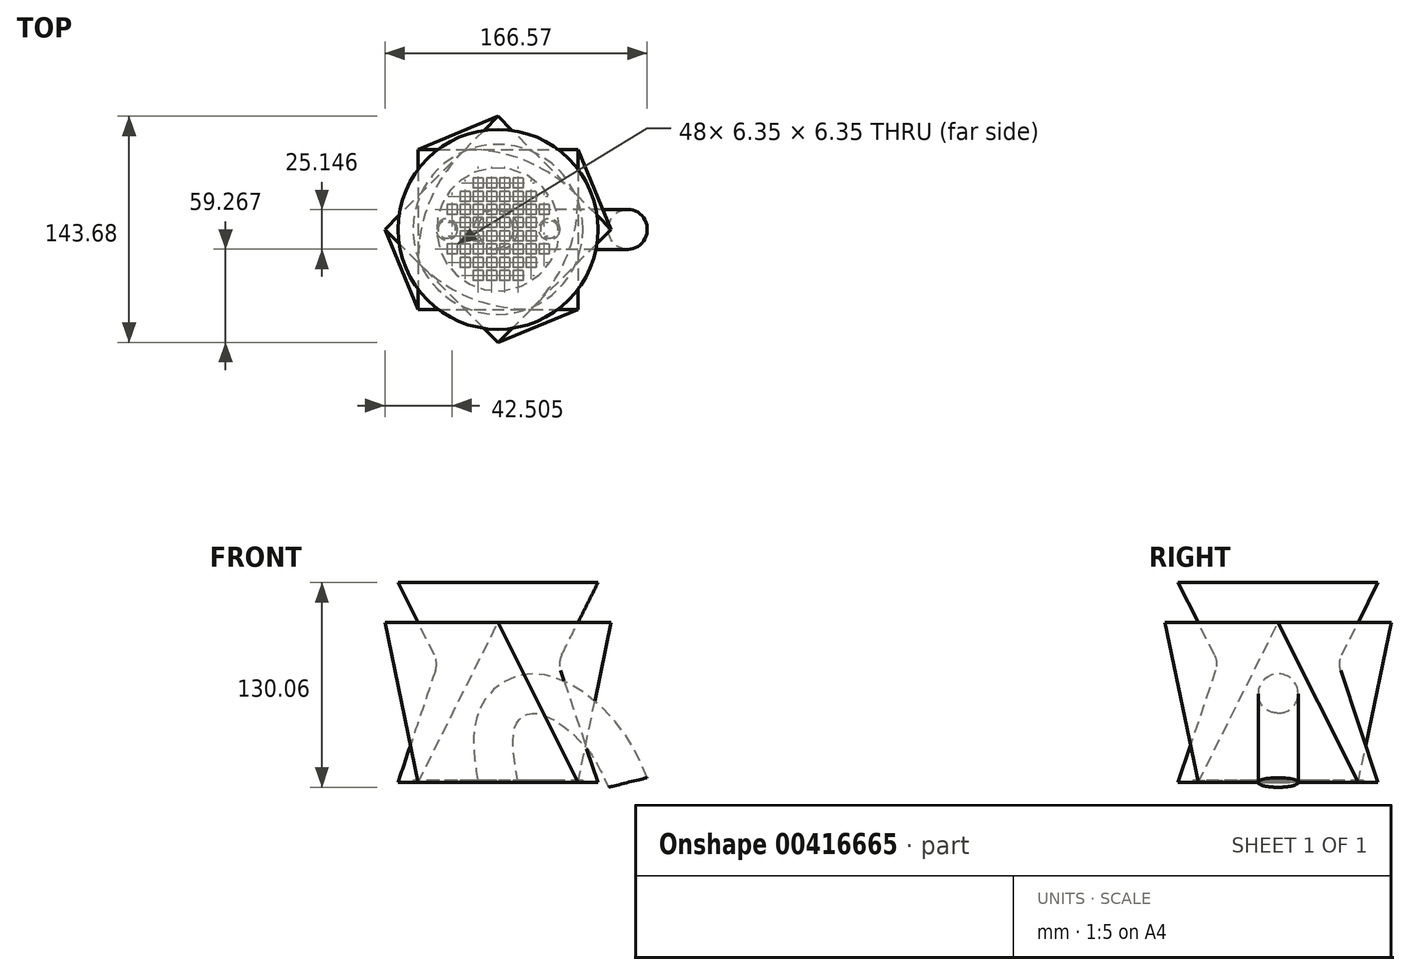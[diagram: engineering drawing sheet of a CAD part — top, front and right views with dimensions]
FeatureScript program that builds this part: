
annotation { "Feature Type Name" : "Feature", "Feature Type Description" : "" }
export const myFeature = defineFeature(function(context is Context, id is Id, definition is map)
    precondition{}
    {
        {
            var Q0;
            Q0=qCreatedBy(makeId("Top.planeOp"),FACE);
            var sketch = newSketch(context, id + "F0", { "sketchPlane" : qUnion([Q0])});
            skCircle(sketch, "E0", {"center": v(0, 0) * mm, "radius": 53.98 * mm});
            skPoint(sketch, "E1.middle", {"position": v(0, 6.35) * mm});
            skPoint(sketch, "E2.middle", {"position": v(-29.34, -29.34) * mm});
            skLineSegment(sketch, "E3.0.2.0", {"start": v(-26.16, -9.4) * mm, "end": v(-26.16, -15.75) * mm});
            skLineSegment(sketch, "E3.0.2.1", {"start": v(-26.16, -9.4) * mm, "end": v(-32.51, -9.4) * mm});
            skLineSegment(sketch, "E3.0.2.2", {"start": v(-32.51, -9.4) * mm, "end": v(-32.51, -15.75) * mm});
            skLineSegment(sketch, "E3.0.2.3", {"start": v(-26.16, -15.75) * mm, "end": v(-32.51, -15.75) * mm});
            skLineSegment(sketch, "E3.0.5.0", {"start": v(-26.16, 15.75) * mm, "end": v(-26.16, 9.4) * mm});
            skLineSegment(sketch, "E3.0.5.1", {"start": v(-26.16, 15.75) * mm, "end": v(-32.51, 15.75) * mm});
            skLineSegment(sketch, "E3.0.5.2", {"start": v(-32.51, 15.75) * mm, "end": v(-32.51, 9.4) * mm});
            skLineSegment(sketch, "E3.0.5.3", {"start": v(-26.16, 9.4) * mm, "end": v(-32.51, 9.4) * mm});
            skLineSegment(sketch, "E3.1.1.0", {"start": v(-17.78, -17.78) * mm, "end": v(-17.78, -24.13) * mm});
            skLineSegment(sketch, "E3.1.1.1", {"start": v(-17.78, -17.78) * mm, "end": v(-24.13, -17.78) * mm});
            skLineSegment(sketch, "E3.1.1.2", {"start": v(-24.13, -17.78) * mm, "end": v(-24.13, -24.13) * mm});
            skLineSegment(sketch, "E3.1.1.3", {"start": v(-17.78, -24.13) * mm, "end": v(-24.13, -24.13) * mm});
            skLineSegment(sketch, "E3.1.2.0", {"start": v(-17.78, -9.4) * mm, "end": v(-17.78, -15.75) * mm});
            skLineSegment(sketch, "E3.1.2.1", {"start": v(-17.78, -9.4) * mm, "end": v(-24.13, -9.4) * mm});
            skLineSegment(sketch, "E3.1.2.2", {"start": v(-24.13, -9.4) * mm, "end": v(-24.13, -15.75) * mm});
            skLineSegment(sketch, "E3.1.2.3", {"start": v(-17.78, -15.75) * mm, "end": v(-24.13, -15.75) * mm});
            skLineSegment(sketch, "E3.1.3.0", {"start": v(-17.78, -1.02) * mm, "end": v(-17.78, -7.37) * mm});
            skLineSegment(sketch, "E3.1.3.1", {"start": v(-17.78, -1.02) * mm, "end": v(-24.13, -1.02) * mm});
            skLineSegment(sketch, "E3.1.3.2", {"start": v(-24.13, -1.02) * mm, "end": v(-24.13, -7.37) * mm});
            skLineSegment(sketch, "E3.1.3.3", {"start": v(-17.78, -7.37) * mm, "end": v(-24.13, -7.37) * mm});
            skLineSegment(sketch, "E3.1.4.0", {"start": v(-17.78, 7.37) * mm, "end": v(-17.78, 1.02) * mm});
            skLineSegment(sketch, "E3.1.4.1", {"start": v(-17.78, 7.37) * mm, "end": v(-24.13, 7.37) * mm});
            skLineSegment(sketch, "E3.1.4.2", {"start": v(-24.13, 7.37) * mm, "end": v(-24.13, 1.02) * mm});
            skLineSegment(sketch, "E3.1.4.3", {"start": v(-17.78, 1.02) * mm, "end": v(-24.13, 1.02) * mm});
            skLineSegment(sketch, "E3.1.5.0", {"start": v(-17.78, 15.75) * mm, "end": v(-17.78, 9.4) * mm});
            skLineSegment(sketch, "E3.1.5.1", {"start": v(-17.78, 15.75) * mm, "end": v(-24.13, 15.75) * mm});
            skLineSegment(sketch, "E3.1.5.2", {"start": v(-24.13, 15.75) * mm, "end": v(-24.13, 9.4) * mm});
            skLineSegment(sketch, "E3.1.5.3", {"start": v(-17.78, 9.4) * mm, "end": v(-24.13, 9.4) * mm});
            skLineSegment(sketch, "E3.1.6.0", {"start": v(-17.78, 24.13) * mm, "end": v(-17.78, 17.78) * mm});
            skLineSegment(sketch, "E3.1.6.1", {"start": v(-17.78, 24.13) * mm, "end": v(-24.13, 24.13) * mm});
            skLineSegment(sketch, "E3.1.6.2", {"start": v(-24.13, 24.13) * mm, "end": v(-24.13, 17.78) * mm});
            skLineSegment(sketch, "E3.1.6.3", {"start": v(-17.78, 17.78) * mm, "end": v(-24.13, 17.78) * mm});
            skLineSegment(sketch, "E3.2.0.0", {"start": v(-9.4, -26.16) * mm, "end": v(-9.4, -32.51) * mm});
            skLineSegment(sketch, "E3.2.0.1", {"start": v(-9.4, -26.16) * mm, "end": v(-15.75, -26.16) * mm});
            skLineSegment(sketch, "E3.2.0.2", {"start": v(-15.75, -26.16) * mm, "end": v(-15.75, -32.51) * mm});
            skLineSegment(sketch, "E3.2.0.3", {"start": v(-9.4, -32.51) * mm, "end": v(-15.75, -32.51) * mm});
            skLineSegment(sketch, "E3.2.1.0", {"start": v(-9.4, -17.78) * mm, "end": v(-9.4, -24.13) * mm});
            skLineSegment(sketch, "E3.2.1.1", {"start": v(-9.4, -17.78) * mm, "end": v(-15.75, -17.78) * mm});
            skLineSegment(sketch, "E3.2.1.2", {"start": v(-15.75, -17.78) * mm, "end": v(-15.75, -24.13) * mm});
            skLineSegment(sketch, "E3.2.1.3", {"start": v(-9.4, -24.13) * mm, "end": v(-15.75, -24.13) * mm});
            skLineSegment(sketch, "E3.2.2.0", {"start": v(-9.4, -9.4) * mm, "end": v(-9.4, -15.75) * mm});
            skLineSegment(sketch, "E3.2.2.1", {"start": v(-9.4, -9.4) * mm, "end": v(-15.75, -9.4) * mm});
            skLineSegment(sketch, "E3.2.2.2", {"start": v(-15.75, -9.4) * mm, "end": v(-15.75, -15.75) * mm});
            skLineSegment(sketch, "E3.2.2.3", {"start": v(-9.4, -15.75) * mm, "end": v(-15.75, -15.75) * mm});
            skLineSegment(sketch, "E3.2.3.0", {"start": v(-9.4, -1.02) * mm, "end": v(-9.4, -7.37) * mm});
            skLineSegment(sketch, "E3.2.3.1", {"start": v(-9.4, -1.02) * mm, "end": v(-15.75, -1.02) * mm});
            skLineSegment(sketch, "E3.2.3.2", {"start": v(-15.75, -1.02) * mm, "end": v(-15.75, -7.37) * mm});
            skLineSegment(sketch, "E3.2.3.3", {"start": v(-9.4, -7.37) * mm, "end": v(-15.75, -7.37) * mm});
            skLineSegment(sketch, "E3.2.4.0", {"start": v(-9.4, 7.37) * mm, "end": v(-9.4, 1.02) * mm});
            skLineSegment(sketch, "E3.2.4.1", {"start": v(-9.4, 7.37) * mm, "end": v(-15.75, 7.37) * mm});
            skLineSegment(sketch, "E3.2.4.2", {"start": v(-15.75, 7.37) * mm, "end": v(-15.75, 1.02) * mm});
            skLineSegment(sketch, "E3.2.4.3", {"start": v(-9.4, 1.02) * mm, "end": v(-15.75, 1.02) * mm});
            skLineSegment(sketch, "E3.2.5.0", {"start": v(-9.4, 15.75) * mm, "end": v(-9.4, 9.4) * mm});
            skLineSegment(sketch, "E3.2.5.1", {"start": v(-9.4, 15.75) * mm, "end": v(-15.75, 15.75) * mm});
            skLineSegment(sketch, "E3.2.5.2", {"start": v(-15.75, 15.75) * mm, "end": v(-15.75, 9.4) * mm});
            skLineSegment(sketch, "E3.2.5.3", {"start": v(-9.4, 9.4) * mm, "end": v(-15.75, 9.4) * mm});
            skLineSegment(sketch, "E3.2.6.0", {"start": v(-9.4, 24.13) * mm, "end": v(-9.4, 17.78) * mm});
            skLineSegment(sketch, "E3.2.6.1", {"start": v(-9.4, 24.13) * mm, "end": v(-15.75, 24.13) * mm});
            skLineSegment(sketch, "E3.2.6.2", {"start": v(-15.75, 24.13) * mm, "end": v(-15.75, 17.78) * mm});
            skLineSegment(sketch, "E3.2.6.3", {"start": v(-9.4, 17.78) * mm, "end": v(-15.75, 17.78) * mm});
            skLineSegment(sketch, "E3.2.7.0", {"start": v(-9.4, 32.51) * mm, "end": v(-9.4, 26.16) * mm});
            skLineSegment(sketch, "E3.2.7.1", {"start": v(-9.4, 32.51) * mm, "end": v(-15.75, 32.51) * mm});
            skLineSegment(sketch, "E3.2.7.2", {"start": v(-15.75, 32.51) * mm, "end": v(-15.75, 26.16) * mm});
            skLineSegment(sketch, "E3.2.7.3", {"start": v(-9.4, 26.16) * mm, "end": v(-15.75, 26.16) * mm});
            skLineSegment(sketch, "E3.3.0.0", {"start": v(-1.01, -26.16) * mm, "end": v(-1.01, -32.51) * mm});
            skLineSegment(sketch, "E3.3.0.1", {"start": v(-1.01, -26.16) * mm, "end": v(-7.36, -26.16) * mm});
            skLineSegment(sketch, "E3.3.0.2", {"start": v(-7.36, -26.16) * mm, "end": v(-7.36, -32.51) * mm});
            skLineSegment(sketch, "E3.3.0.3", {"start": v(-1.01, -32.51) * mm, "end": v(-7.36, -32.51) * mm});
            skLineSegment(sketch, "E3.3.1.0", {"start": v(-1.01, -17.78) * mm, "end": v(-1.01, -24.13) * mm});
            skLineSegment(sketch, "E3.3.1.1", {"start": v(-1.01, -17.78) * mm, "end": v(-7.36, -17.78) * mm});
            skLineSegment(sketch, "E3.3.1.2", {"start": v(-7.36, -17.78) * mm, "end": v(-7.36, -24.13) * mm});
            skLineSegment(sketch, "E3.3.1.3", {"start": v(-1.01, -24.13) * mm, "end": v(-7.36, -24.13) * mm});
            skLineSegment(sketch, "E3.3.2.0", {"start": v(-1.01, -9.4) * mm, "end": v(-1.01, -15.75) * mm});
            skLineSegment(sketch, "E3.3.2.1", {"start": v(-1.01, -9.4) * mm, "end": v(-7.36, -9.4) * mm});
            skLineSegment(sketch, "E3.3.2.2", {"start": v(-7.36, -9.4) * mm, "end": v(-7.36, -15.75) * mm});
            skLineSegment(sketch, "E3.3.2.3", {"start": v(-1.01, -15.75) * mm, "end": v(-7.36, -15.75) * mm});
            skLineSegment(sketch, "E3.3.3.0", {"start": v(-1.01, -1.02) * mm, "end": v(-1.01, -7.37) * mm});
            skLineSegment(sketch, "E3.3.3.1", {"start": v(-1.01, -1.02) * mm, "end": v(-7.36, -1.02) * mm});
            skLineSegment(sketch, "E3.3.3.2", {"start": v(-7.36, -1.02) * mm, "end": v(-7.36, -7.37) * mm});
            skLineSegment(sketch, "E3.3.3.3", {"start": v(-1.01, -7.37) * mm, "end": v(-7.36, -7.37) * mm});
            skLineSegment(sketch, "E3.3.4.0", {"start": v(-1.01, 7.37) * mm, "end": v(-1.01, 1.02) * mm});
            skLineSegment(sketch, "E3.3.4.1", {"start": v(-1.01, 7.37) * mm, "end": v(-7.36, 7.37) * mm});
            skLineSegment(sketch, "E3.3.4.2", {"start": v(-7.36, 7.37) * mm, "end": v(-7.36, 1.02) * mm});
            skLineSegment(sketch, "E3.3.4.3", {"start": v(-1.01, 1.02) * mm, "end": v(-7.36, 1.02) * mm});
            skLineSegment(sketch, "E3.3.5.0", {"start": v(-1.01, 15.75) * mm, "end": v(-1.01, 9.4) * mm});
            skLineSegment(sketch, "E3.3.5.1", {"start": v(-1.01, 15.75) * mm, "end": v(-7.36, 15.75) * mm});
            skLineSegment(sketch, "E3.3.5.2", {"start": v(-7.36, 15.75) * mm, "end": v(-7.36, 9.4) * mm});
            skLineSegment(sketch, "E3.3.5.3", {"start": v(-1.01, 9.4) * mm, "end": v(-7.36, 9.4) * mm});
            skLineSegment(sketch, "E3.3.6.0", {"start": v(-1.01, 24.13) * mm, "end": v(-1.01, 17.78) * mm});
            skLineSegment(sketch, "E3.3.6.1", {"start": v(-1.01, 24.13) * mm, "end": v(-7.36, 24.13) * mm});
            skLineSegment(sketch, "E3.3.6.2", {"start": v(-7.36, 24.13) * mm, "end": v(-7.36, 17.78) * mm});
            skLineSegment(sketch, "E3.3.6.3", {"start": v(-1.01, 17.78) * mm, "end": v(-7.36, 17.78) * mm});
            skLineSegment(sketch, "E3.3.7.0", {"start": v(-1.01, 32.51) * mm, "end": v(-1.01, 26.16) * mm});
            skLineSegment(sketch, "E3.3.7.1", {"start": v(-1.01, 32.51) * mm, "end": v(-7.36, 32.51) * mm});
            skLineSegment(sketch, "E3.3.7.2", {"start": v(-7.36, 32.51) * mm, "end": v(-7.36, 26.16) * mm});
            skLineSegment(sketch, "E3.3.7.3", {"start": v(-1.01, 26.16) * mm, "end": v(-7.36, 26.16) * mm});
            skLineSegment(sketch, "E3.4.0.0", {"start": v(7.37, -26.16) * mm, "end": v(7.37, -32.51) * mm});
            skLineSegment(sketch, "E3.4.0.1", {"start": v(7.37, -26.16) * mm, "end": v(1.02, -26.16) * mm});
            skLineSegment(sketch, "E3.4.0.2", {"start": v(1.02, -26.16) * mm, "end": v(1.02, -32.51) * mm});
            skLineSegment(sketch, "E3.4.0.3", {"start": v(7.37, -32.51) * mm, "end": v(1.02, -32.51) * mm});
            skLineSegment(sketch, "E3.4.1.0", {"start": v(7.37, -17.78) * mm, "end": v(7.37, -24.13) * mm});
            skLineSegment(sketch, "E3.4.1.1", {"start": v(7.37, -17.78) * mm, "end": v(1.02, -17.78) * mm});
            skLineSegment(sketch, "E3.4.1.2", {"start": v(1.02, -17.78) * mm, "end": v(1.02, -24.13) * mm});
            skLineSegment(sketch, "E3.4.1.3", {"start": v(7.37, -24.13) * mm, "end": v(1.02, -24.13) * mm});
            skLineSegment(sketch, "E3.4.2.0", {"start": v(7.37, -9.4) * mm, "end": v(7.37, -15.75) * mm});
            skLineSegment(sketch, "E3.4.2.1", {"start": v(7.37, -9.4) * mm, "end": v(1.02, -9.4) * mm});
            skLineSegment(sketch, "E3.4.2.2", {"start": v(1.02, -9.4) * mm, "end": v(1.02, -15.75) * mm});
            skLineSegment(sketch, "E3.4.2.3", {"start": v(7.37, -15.75) * mm, "end": v(1.02, -15.75) * mm});
            skLineSegment(sketch, "E3.4.3.0", {"start": v(7.37, -1.02) * mm, "end": v(7.37, -7.37) * mm});
            skLineSegment(sketch, "E3.4.3.1", {"start": v(7.37, -1.02) * mm, "end": v(1.02, -1.02) * mm});
            skLineSegment(sketch, "E3.4.3.2", {"start": v(1.02, -1.02) * mm, "end": v(1.02, -7.37) * mm});
            skLineSegment(sketch, "E3.4.3.3", {"start": v(7.37, -7.37) * mm, "end": v(1.02, -7.37) * mm});
            skLineSegment(sketch, "E3.4.4.0", {"start": v(7.37, 7.37) * mm, "end": v(7.37, 1.02) * mm});
            skLineSegment(sketch, "E3.4.4.1", {"start": v(7.37, 7.37) * mm, "end": v(1.02, 7.37) * mm});
            skLineSegment(sketch, "E3.4.4.2", {"start": v(1.02, 7.37) * mm, "end": v(1.02, 1.02) * mm});
            skLineSegment(sketch, "E3.4.4.3", {"start": v(7.37, 1.02) * mm, "end": v(1.02, 1.02) * mm});
            skLineSegment(sketch, "E3.4.5.0", {"start": v(7.37, 15.75) * mm, "end": v(7.37, 9.4) * mm});
            skLineSegment(sketch, "E3.4.5.1", {"start": v(7.37, 15.75) * mm, "end": v(1.02, 15.75) * mm});
            skLineSegment(sketch, "E3.4.5.2", {"start": v(1.02, 15.75) * mm, "end": v(1.02, 9.4) * mm});
            skLineSegment(sketch, "E3.4.5.3", {"start": v(7.37, 9.4) * mm, "end": v(1.02, 9.4) * mm});
            skLineSegment(sketch, "E3.4.6.0", {"start": v(7.37, 24.13) * mm, "end": v(7.37, 17.78) * mm});
            skLineSegment(sketch, "E3.4.6.1", {"start": v(7.37, 24.13) * mm, "end": v(1.02, 24.13) * mm});
            skLineSegment(sketch, "E3.4.6.2", {"start": v(1.02, 24.13) * mm, "end": v(1.02, 17.78) * mm});
            skLineSegment(sketch, "E3.4.6.3", {"start": v(7.37, 17.78) * mm, "end": v(1.02, 17.78) * mm});
            skLineSegment(sketch, "E3.4.7.0", {"start": v(7.37, 32.51) * mm, "end": v(7.37, 26.16) * mm});
            skLineSegment(sketch, "E3.4.7.1", {"start": v(7.37, 32.51) * mm, "end": v(1.02, 32.51) * mm});
            skLineSegment(sketch, "E3.4.7.2", {"start": v(1.02, 32.51) * mm, "end": v(1.02, 26.16) * mm});
            skLineSegment(sketch, "E3.4.7.3", {"start": v(7.37, 26.16) * mm, "end": v(1.02, 26.16) * mm});
            skLineSegment(sketch, "E3.5.0.0", {"start": v(15.75, -26.16) * mm, "end": v(15.75, -32.51) * mm});
            skLineSegment(sketch, "E3.5.0.1", {"start": v(15.75, -26.16) * mm, "end": v(9.4, -26.16) * mm});
            skLineSegment(sketch, "E3.5.0.2", {"start": v(9.4, -26.16) * mm, "end": v(9.4, -32.51) * mm});
            skLineSegment(sketch, "E3.5.0.3", {"start": v(15.75, -32.51) * mm, "end": v(9.4, -32.51) * mm});
            skLineSegment(sketch, "E3.5.1.0", {"start": v(15.75, -17.78) * mm, "end": v(15.75, -24.13) * mm});
            skLineSegment(sketch, "E3.5.1.1", {"start": v(15.75, -17.78) * mm, "end": v(9.4, -17.78) * mm});
            skLineSegment(sketch, "E3.5.1.2", {"start": v(9.4, -17.78) * mm, "end": v(9.4, -24.13) * mm});
            skLineSegment(sketch, "E3.5.1.3", {"start": v(15.75, -24.13) * mm, "end": v(9.4, -24.13) * mm});
            skLineSegment(sketch, "E3.5.2.0", {"start": v(15.75, -9.4) * mm, "end": v(15.75, -15.75) * mm});
            skLineSegment(sketch, "E3.5.2.1", {"start": v(15.75, -9.4) * mm, "end": v(9.4, -9.4) * mm});
            skLineSegment(sketch, "E3.5.2.2", {"start": v(9.4, -9.4) * mm, "end": v(9.4, -15.75) * mm});
            skLineSegment(sketch, "E3.5.2.3", {"start": v(15.75, -15.75) * mm, "end": v(9.4, -15.75) * mm});
            skLineSegment(sketch, "E3.5.3.0", {"start": v(15.75, -1.02) * mm, "end": v(15.75, -7.37) * mm});
            skLineSegment(sketch, "E3.5.3.1", {"start": v(15.75, -1.02) * mm, "end": v(9.4, -1.02) * mm});
            skLineSegment(sketch, "E3.5.3.2", {"start": v(9.4, -1.02) * mm, "end": v(9.4, -7.37) * mm});
            skLineSegment(sketch, "E3.5.3.3", {"start": v(15.75, -7.37) * mm, "end": v(9.4, -7.37) * mm});
            skLineSegment(sketch, "E3.5.4.0", {"start": v(15.75, 7.37) * mm, "end": v(15.75, 1.02) * mm});
            skLineSegment(sketch, "E3.5.4.1", {"start": v(15.75, 7.37) * mm, "end": v(9.4, 7.37) * mm});
            skLineSegment(sketch, "E3.5.4.2", {"start": v(9.4, 7.37) * mm, "end": v(9.4, 1.02) * mm});
            skLineSegment(sketch, "E3.5.4.3", {"start": v(15.75, 1.02) * mm, "end": v(9.4, 1.02) * mm});
            skLineSegment(sketch, "E3.5.5.0", {"start": v(15.75, 15.75) * mm, "end": v(15.75, 9.4) * mm});
            skLineSegment(sketch, "E3.5.5.1", {"start": v(15.75, 15.75) * mm, "end": v(9.4, 15.75) * mm});
            skLineSegment(sketch, "E3.5.5.2", {"start": v(9.4, 15.75) * mm, "end": v(9.4, 9.4) * mm});
            skLineSegment(sketch, "E3.5.5.3", {"start": v(15.75, 9.4) * mm, "end": v(9.4, 9.4) * mm});
            skLineSegment(sketch, "E3.5.6.0", {"start": v(15.75, 24.13) * mm, "end": v(15.75, 17.78) * mm});
            skLineSegment(sketch, "E3.5.6.1", {"start": v(15.75, 24.13) * mm, "end": v(9.4, 24.13) * mm});
            skLineSegment(sketch, "E3.5.6.2", {"start": v(9.4, 24.13) * mm, "end": v(9.4, 17.78) * mm});
            skLineSegment(sketch, "E3.5.6.3", {"start": v(15.75, 17.78) * mm, "end": v(9.4, 17.78) * mm});
            skLineSegment(sketch, "E3.5.7.0", {"start": v(15.75, 32.51) * mm, "end": v(15.75, 26.16) * mm});
            skLineSegment(sketch, "E3.5.7.1", {"start": v(15.75, 32.51) * mm, "end": v(9.4, 32.51) * mm});
            skLineSegment(sketch, "E3.5.7.2", {"start": v(9.4, 32.51) * mm, "end": v(9.4, 26.16) * mm});
            skLineSegment(sketch, "E3.5.7.3", {"start": v(15.75, 26.16) * mm, "end": v(9.4, 26.16) * mm});
            skLineSegment(sketch, "E3.6.1.0", {"start": v(24.13, -17.78) * mm, "end": v(24.13, -24.13) * mm});
            skLineSegment(sketch, "E3.6.1.1", {"start": v(24.13, -17.78) * mm, "end": v(17.78, -17.78) * mm});
            skLineSegment(sketch, "E3.6.1.2", {"start": v(17.78, -17.78) * mm, "end": v(17.78, -24.13) * mm});
            skLineSegment(sketch, "E3.6.1.3", {"start": v(24.13, -24.13) * mm, "end": v(17.78, -24.13) * mm});
            skLineSegment(sketch, "E3.6.2.0", {"start": v(24.13, -9.4) * mm, "end": v(24.13, -15.75) * mm});
            skLineSegment(sketch, "E3.6.2.1", {"start": v(24.13, -9.4) * mm, "end": v(17.78, -9.4) * mm});
            skLineSegment(sketch, "E3.6.2.2", {"start": v(17.78, -9.4) * mm, "end": v(17.78, -15.75) * mm});
            skLineSegment(sketch, "E3.6.2.3", {"start": v(24.13, -15.75) * mm, "end": v(17.78, -15.75) * mm});
            skLineSegment(sketch, "E3.6.3.0", {"start": v(24.13, -1.02) * mm, "end": v(24.13, -7.37) * mm});
            skLineSegment(sketch, "E3.6.3.1", {"start": v(24.13, -1.02) * mm, "end": v(17.78, -1.02) * mm});
            skLineSegment(sketch, "E3.6.3.2", {"start": v(17.78, -1.02) * mm, "end": v(17.78, -7.37) * mm});
            skLineSegment(sketch, "E3.6.3.3", {"start": v(24.13, -7.37) * mm, "end": v(17.78, -7.37) * mm});
            skLineSegment(sketch, "E3.6.4.0", {"start": v(24.13, 7.37) * mm, "end": v(24.13, 1.02) * mm});
            skLineSegment(sketch, "E3.6.4.1", {"start": v(24.13, 7.37) * mm, "end": v(17.78, 7.37) * mm});
            skLineSegment(sketch, "E3.6.4.2", {"start": v(17.78, 7.37) * mm, "end": v(17.78, 1.02) * mm});
            skLineSegment(sketch, "E3.6.4.3", {"start": v(24.13, 1.02) * mm, "end": v(17.78, 1.02) * mm});
            skLineSegment(sketch, "E3.6.5.0", {"start": v(24.13, 15.75) * mm, "end": v(24.13, 9.4) * mm});
            skLineSegment(sketch, "E3.6.5.1", {"start": v(24.13, 15.75) * mm, "end": v(17.78, 15.75) * mm});
            skLineSegment(sketch, "E3.6.5.2", {"start": v(17.78, 15.75) * mm, "end": v(17.78, 9.4) * mm});
            skLineSegment(sketch, "E3.6.5.3", {"start": v(24.13, 9.4) * mm, "end": v(17.78, 9.4) * mm});
            skLineSegment(sketch, "E3.6.6.0", {"start": v(24.13, 24.13) * mm, "end": v(24.13, 17.78) * mm});
            skLineSegment(sketch, "E3.6.6.1", {"start": v(24.13, 24.13) * mm, "end": v(17.78, 24.13) * mm});
            skLineSegment(sketch, "E3.6.6.2", {"start": v(17.78, 24.13) * mm, "end": v(17.78, 17.78) * mm});
            skLineSegment(sketch, "E3.6.6.3", {"start": v(24.13, 17.78) * mm, "end": v(17.78, 17.78) * mm});
            skLineSegment(sketch, "E3.7.2.0", {"start": v(32.51, -9.4) * mm, "end": v(32.51, -15.75) * mm});
            skLineSegment(sketch, "E3.7.2.1", {"start": v(32.51, -9.4) * mm, "end": v(26.16, -9.4) * mm});
            skLineSegment(sketch, "E3.7.2.2", {"start": v(26.16, -9.4) * mm, "end": v(26.16, -15.75) * mm});
            skLineSegment(sketch, "E3.7.2.3", {"start": v(32.51, -15.75) * mm, "end": v(26.16, -15.75) * mm});
            skLineSegment(sketch, "E3.7.5.0", {"start": v(32.51, 15.75) * mm, "end": v(32.51, 9.4) * mm});
            skLineSegment(sketch, "E3.7.5.1", {"start": v(32.51, 15.75) * mm, "end": v(26.16, 15.75) * mm});
            skLineSegment(sketch, "E3.7.5.2", {"start": v(26.16, 15.75) * mm, "end": v(26.16, 9.4) * mm});
            skLineSegment(sketch, "E3.7.5.3", {"start": v(32.51, 9.4) * mm, "end": v(26.16, 9.4) * mm});
            skPoint(sketch, "E4.middle", {"position": v(1.02, 1.02) * mm});
            skLineSegment(sketch, "E5", {"start": v(32.51, 9.4) * mm, "end": v(32.51, -9.4) * mm, "construction": true});
            skLineSegment(sketch, "E6", {"start": v(-32.51, 9.4) * mm, "end": v(-32.51, -9.4) * mm, "construction": true});
            skLineSegment(sketch, "E7", {"start": v(0, 0) * mm, "end": v(-49.5, 0) * mm, "construction": true});
            skLineSegment(sketch, "E8", {"start": v(0, 0) * mm, "end": v(53.98, 0) * mm, "construction": true});
            skSolve(sketch);
        }
        {
            var Q0;
            Q0=makeQuery(id+"F0.imprint","IMPRINT",FACE,{"disambiguationData":[TD([[makeQuery(id+"F0.imprint","IMPRINT",EDGE,{"derivedFrom":sQuery(id+"F0.wireOp",EDGE,"E0")}),1.0]])]});
            extrude(context, id + "F1", {"entities" : qUnion([Q0]), "depth" : 1.27 * mm});
        }
        {
            var Q0;
            Q0=makeQuery(id+"F1.opExtrude","CAP_FACE",FACE,{"disambiguationData":[OSD([sQuery(id+"F0.wireOp",EDGE,"E0"),sQuery(id+"F0.wireOp",EDGE,"E3.0.2.0"),sQuery(id+"F0.wireOp",EDGE,"E3.0.2.1"),sQuery(id+"F0.wireOp",EDGE,"E3.0.2.2"),sQuery(id+"F0.wireOp",EDGE,"E3.0.2.3"),sQuery(id+"F0.wireOp",EDGE,"E3.0.5.0"),sQuery(id+"F0.wireOp",EDGE,"E3.0.5.1"),sQuery(id+"F0.wireOp",EDGE,"E3.0.5.2"),sQuery(id+"F0.wireOp",EDGE,"E3.0.5.3"),sQuery(id+"F0.wireOp",EDGE,"E3.1.1.0"),sQuery(id+"F0.wireOp",EDGE,"E3.1.1.1"),sQuery(id+"F0.wireOp",EDGE,"E3.1.1.2"),sQuery(id+"F0.wireOp",EDGE,"E3.1.1.3"),sQuery(id+"F0.wireOp",EDGE,"E3.1.2.0"),sQuery(id+"F0.wireOp",EDGE,"E3.1.2.1"),sQuery(id+"F0.wireOp",EDGE,"E3.1.2.2"),sQuery(id+"F0.wireOp",EDGE,"E3.1.2.3"),sQuery(id+"F0.wireOp",EDGE,"E3.1.3.0"),sQuery(id+"F0.wireOp",EDGE,"E3.1.3.1"),sQuery(id+"F0.wireOp",EDGE,"E3.1.3.2"),sQuery(id+"F0.wireOp",EDGE,"E3.1.3.3"),sQuery(id+"F0.wireOp",EDGE,"E3.1.4.0"),sQuery(id+"F0.wireOp",EDGE,"E3.1.4.1"),sQuery(id+"F0.wireOp",EDGE,"E3.1.4.2"),sQuery(id+"F0.wireOp",EDGE,"E3.1.4.3"),sQuery(id+"F0.wireOp",EDGE,"E3.1.5.0"),sQuery(id+"F0.wireOp",EDGE,"E3.1.5.1"),sQuery(id+"F0.wireOp",EDGE,"E3.1.5.2"),sQuery(id+"F0.wireOp",EDGE,"E3.1.5.3"),sQuery(id+"F0.wireOp",EDGE,"E3.1.6.0"),sQuery(id+"F0.wireOp",EDGE,"E3.1.6.1"),sQuery(id+"F0.wireOp",EDGE,"E3.1.6.2"),sQuery(id+"F0.wireOp",EDGE,"E3.1.6.3"),sQuery(id+"F0.wireOp",EDGE,"E3.2.0.0"),sQuery(id+"F0.wireOp",EDGE,"E3.2.0.1"),sQuery(id+"F0.wireOp",EDGE,"E3.2.0.2"),sQuery(id+"F0.wireOp",EDGE,"E3.2.0.3"),sQuery(id+"F0.wireOp",EDGE,"E3.2.1.0"),sQuery(id+"F0.wireOp",EDGE,"E3.2.1.1"),sQuery(id+"F0.wireOp",EDGE,"E3.2.1.2"),sQuery(id+"F0.wireOp",EDGE,"E3.2.1.3"),sQuery(id+"F0.wireOp",EDGE,"E3.2.2.0"),sQuery(id+"F0.wireOp",EDGE,"E3.2.2.1"),sQuery(id+"F0.wireOp",EDGE,"E3.2.2.2"),sQuery(id+"F0.wireOp",EDGE,"E3.2.2.3"),sQuery(id+"F0.wireOp",EDGE,"E3.2.3.0"),sQuery(id+"F0.wireOp",EDGE,"E3.2.3.1"),sQuery(id+"F0.wireOp",EDGE,"E3.2.3.2"),sQuery(id+"F0.wireOp",EDGE,"E3.2.3.3"),sQuery(id+"F0.wireOp",EDGE,"E3.2.4.0"),sQuery(id+"F0.wireOp",EDGE,"E3.2.4.1"),sQuery(id+"F0.wireOp",EDGE,"E3.2.4.2"),sQuery(id+"F0.wireOp",EDGE,"E3.2.4.3"),sQuery(id+"F0.wireOp",EDGE,"E3.2.5.0"),sQuery(id+"F0.wireOp",EDGE,"E3.2.5.1"),sQuery(id+"F0.wireOp",EDGE,"E3.2.5.2"),sQuery(id+"F0.wireOp",EDGE,"E3.2.5.3"),sQuery(id+"F0.wireOp",EDGE,"E3.2.6.0"),sQuery(id+"F0.wireOp",EDGE,"E3.2.6.1"),sQuery(id+"F0.wireOp",EDGE,"E3.2.6.2"),sQuery(id+"F0.wireOp",EDGE,"E3.2.6.3"),sQuery(id+"F0.wireOp",EDGE,"E3.2.7.0"),sQuery(id+"F0.wireOp",EDGE,"E3.2.7.1"),sQuery(id+"F0.wireOp",EDGE,"E3.2.7.2"),sQuery(id+"F0.wireOp",EDGE,"E3.2.7.3"),sQuery(id+"F0.wireOp",EDGE,"E3.3.0.0"),sQuery(id+"F0.wireOp",EDGE,"E3.3.0.1"),sQuery(id+"F0.wireOp",EDGE,"E3.3.0.2"),sQuery(id+"F0.wireOp",EDGE,"E3.3.0.3"),sQuery(id+"F0.wireOp",EDGE,"E3.3.1.0"),sQuery(id+"F0.wireOp",EDGE,"E3.3.1.1"),sQuery(id+"F0.wireOp",EDGE,"E3.3.1.2"),sQuery(id+"F0.wireOp",EDGE,"E3.3.1.3"),sQuery(id+"F0.wireOp",EDGE,"E3.3.2.0"),sQuery(id+"F0.wireOp",EDGE,"E3.3.2.1"),sQuery(id+"F0.wireOp",EDGE,"E3.3.2.2"),sQuery(id+"F0.wireOp",EDGE,"E3.3.2.3"),sQuery(id+"F0.wireOp",EDGE,"E3.3.3.0"),sQuery(id+"F0.wireOp",EDGE,"E3.3.3.1"),sQuery(id+"F0.wireOp",EDGE,"E3.3.3.2"),sQuery(id+"F0.wireOp",EDGE,"E3.3.3.3"),sQuery(id+"F0.wireOp",EDGE,"E3.3.4.0"),sQuery(id+"F0.wireOp",EDGE,"E3.3.4.1"),sQuery(id+"F0.wireOp",EDGE,"E3.3.4.2"),sQuery(id+"F0.wireOp",EDGE,"E3.3.4.3"),sQuery(id+"F0.wireOp",EDGE,"E3.3.5.0"),sQuery(id+"F0.wireOp",EDGE,"E3.3.5.1"),sQuery(id+"F0.wireOp",EDGE,"E3.3.5.2"),sQuery(id+"F0.wireOp",EDGE,"E3.3.5.3"),sQuery(id+"F0.wireOp",EDGE,"E3.3.6.0"),sQuery(id+"F0.wireOp",EDGE,"E3.3.6.1"),sQuery(id+"F0.wireOp",EDGE,"E3.3.6.2"),sQuery(id+"F0.wireOp",EDGE,"E3.3.6.3"),sQuery(id+"F0.wireOp",EDGE,"E3.3.7.0"),sQuery(id+"F0.wireOp",EDGE,"E3.3.7.1"),sQuery(id+"F0.wireOp",EDGE,"E3.3.7.2"),sQuery(id+"F0.wireOp",EDGE,"E3.3.7.3"),sQuery(id+"F0.wireOp",EDGE,"E3.4.0.0"),sQuery(id+"F0.wireOp",EDGE,"E3.4.0.1"),sQuery(id+"F0.wireOp",EDGE,"E3.4.0.2"),sQuery(id+"F0.wireOp",EDGE,"E3.4.0.3"),sQuery(id+"F0.wireOp",EDGE,"E3.4.1.0"),sQuery(id+"F0.wireOp",EDGE,"E3.4.1.1"),sQuery(id+"F0.wireOp",EDGE,"E3.4.1.2"),sQuery(id+"F0.wireOp",EDGE,"E3.4.1.3"),sQuery(id+"F0.wireOp",EDGE,"E3.4.2.0"),sQuery(id+"F0.wireOp",EDGE,"E3.4.2.1"),sQuery(id+"F0.wireOp",EDGE,"E3.4.2.2"),sQuery(id+"F0.wireOp",EDGE,"E3.4.2.3"),sQuery(id+"F0.wireOp",EDGE,"E3.4.3.0"),sQuery(id+"F0.wireOp",EDGE,"E3.4.3.1"),sQuery(id+"F0.wireOp",EDGE,"E3.4.3.2"),sQuery(id+"F0.wireOp",EDGE,"E3.4.3.3"),sQuery(id+"F0.wireOp",EDGE,"E3.4.4.0"),sQuery(id+"F0.wireOp",EDGE,"E3.4.4.1"),sQuery(id+"F0.wireOp",EDGE,"E3.4.4.2"),sQuery(id+"F0.wireOp",EDGE,"E3.4.4.3"),sQuery(id+"F0.wireOp",EDGE,"E3.4.5.0"),sQuery(id+"F0.wireOp",EDGE,"E3.4.5.1"),sQuery(id+"F0.wireOp",EDGE,"E3.4.5.2"),sQuery(id+"F0.wireOp",EDGE,"E3.4.5.3"),sQuery(id+"F0.wireOp",EDGE,"E3.4.6.0"),sQuery(id+"F0.wireOp",EDGE,"E3.4.6.1"),sQuery(id+"F0.wireOp",EDGE,"E3.4.6.2"),sQuery(id+"F0.wireOp",EDGE,"E3.4.6.3"),sQuery(id+"F0.wireOp",EDGE,"E3.4.7.0"),sQuery(id+"F0.wireOp",EDGE,"E3.4.7.1"),sQuery(id+"F0.wireOp",EDGE,"E3.4.7.2"),sQuery(id+"F0.wireOp",EDGE,"E3.4.7.3"),sQuery(id+"F0.wireOp",EDGE,"E3.5.0.0"),sQuery(id+"F0.wireOp",EDGE,"E3.5.0.1"),sQuery(id+"F0.wireOp",EDGE,"E3.5.0.2"),sQuery(id+"F0.wireOp",EDGE,"E3.5.0.3"),sQuery(id+"F0.wireOp",EDGE,"E3.5.1.0"),sQuery(id+"F0.wireOp",EDGE,"E3.5.1.1"),sQuery(id+"F0.wireOp",EDGE,"E3.5.1.2"),sQuery(id+"F0.wireOp",EDGE,"E3.5.1.3"),sQuery(id+"F0.wireOp",EDGE,"E3.5.2.0"),sQuery(id+"F0.wireOp",EDGE,"E3.5.2.1"),sQuery(id+"F0.wireOp",EDGE,"E3.5.2.2"),sQuery(id+"F0.wireOp",EDGE,"E3.5.2.3"),sQuery(id+"F0.wireOp",EDGE,"E3.5.3.0"),sQuery(id+"F0.wireOp",EDGE,"E3.5.3.1"),sQuery(id+"F0.wireOp",EDGE,"E3.5.3.2"),sQuery(id+"F0.wireOp",EDGE,"E3.5.3.3"),sQuery(id+"F0.wireOp",EDGE,"E3.5.4.0"),sQuery(id+"F0.wireOp",EDGE,"E3.5.4.1"),sQuery(id+"F0.wireOp",EDGE,"E3.5.4.2"),sQuery(id+"F0.wireOp",EDGE,"E3.5.4.3"),sQuery(id+"F0.wireOp",EDGE,"E3.5.5.0"),sQuery(id+"F0.wireOp",EDGE,"E3.5.5.1"),sQuery(id+"F0.wireOp",EDGE,"E3.5.5.2"),sQuery(id+"F0.wireOp",EDGE,"E3.5.5.3"),sQuery(id+"F0.wireOp",EDGE,"E3.5.6.0"),sQuery(id+"F0.wireOp",EDGE,"E3.5.6.1"),sQuery(id+"F0.wireOp",EDGE,"E3.5.6.2"),sQuery(id+"F0.wireOp",EDGE,"E3.5.6.3"),sQuery(id+"F0.wireOp",EDGE,"E3.5.7.0"),sQuery(id+"F0.wireOp",EDGE,"E3.5.7.1"),sQuery(id+"F0.wireOp",EDGE,"E3.5.7.2"),sQuery(id+"F0.wireOp",EDGE,"E3.5.7.3"),sQuery(id+"F0.wireOp",EDGE,"E3.6.1.0"),sQuery(id+"F0.wireOp",EDGE,"E3.6.1.1"),sQuery(id+"F0.wireOp",EDGE,"E3.6.1.2"),sQuery(id+"F0.wireOp",EDGE,"E3.6.1.3"),sQuery(id+"F0.wireOp",EDGE,"E3.6.2.0"),sQuery(id+"F0.wireOp",EDGE,"E3.6.2.1"),sQuery(id+"F0.wireOp",EDGE,"E3.6.2.2"),sQuery(id+"F0.wireOp",EDGE,"E3.6.2.3"),sQuery(id+"F0.wireOp",EDGE,"E3.6.3.0"),sQuery(id+"F0.wireOp",EDGE,"E3.6.3.1"),sQuery(id+"F0.wireOp",EDGE,"E3.6.3.2"),sQuery(id+"F0.wireOp",EDGE,"E3.6.3.3"),sQuery(id+"F0.wireOp",EDGE,"E3.6.4.0"),sQuery(id+"F0.wireOp",EDGE,"E3.6.4.1"),sQuery(id+"F0.wireOp",EDGE,"E3.6.4.2"),sQuery(id+"F0.wireOp",EDGE,"E3.6.4.3"),sQuery(id+"F0.wireOp",EDGE,"E3.6.5.0"),sQuery(id+"F0.wireOp",EDGE,"E3.6.5.1"),sQuery(id+"F0.wireOp",EDGE,"E3.6.5.2"),sQuery(id+"F0.wireOp",EDGE,"E3.6.5.3"),sQuery(id+"F0.wireOp",EDGE,"E3.6.6.0"),sQuery(id+"F0.wireOp",EDGE,"E3.6.6.1"),sQuery(id+"F0.wireOp",EDGE,"E3.6.6.2"),sQuery(id+"F0.wireOp",EDGE,"E3.6.6.3"),sQuery(id+"F0.wireOp",EDGE,"E3.7.2.0"),sQuery(id+"F0.wireOp",EDGE,"E3.7.2.1"),sQuery(id+"F0.wireOp",EDGE,"E3.7.2.2"),sQuery(id+"F0.wireOp",EDGE,"E3.7.2.3"),sQuery(id+"F0.wireOp",EDGE,"E3.7.5.0"),sQuery(id+"F0.wireOp",EDGE,"E3.7.5.1"),sQuery(id+"F0.wireOp",EDGE,"E3.7.5.2"),sQuery(id+"F0.wireOp",EDGE,"E3.7.5.3")])],"isStart":false});
            var sketch = newSketch(context, id + "F2", { "sketchPlane" : qUnion([Q0])});
            skPoint(sketch, "E9.endSnap0", {"position": v(-32.51, 0) * mm});
            skCircle(sketch, "E10", {"center": v(-32.53, -0.04) * mm, "radius": 3.18 * mm});
            skCircle(sketch, "E11", {"center": v(32.51, 0) * mm, "radius": 3.18 * mm});
            skSolve(sketch);
        }
        {
            var Q0;
            Q0=sQuery(id+"F2.wireOp",VERTEX,"E11.center");
            var Q1;
            Q1=sQuery(id+"F2.wireOp",VERTEX,"E9.endSnap0");
            var Q2;
            Q2=makeQuery(id+"F1.opExtrude","SWEPT_BODY",BODY,{"disambiguationData":[OSD([sQuery(id+"F0.wireOp",EDGE,"E0"),sQuery(id+"F0.wireOp",EDGE,"E3.0.2.0"),sQuery(id+"F0.wireOp",EDGE,"E3.0.2.1"),sQuery(id+"F0.wireOp",EDGE,"E3.0.2.2"),sQuery(id+"F0.wireOp",EDGE,"E3.0.2.3"),sQuery(id+"F0.wireOp",EDGE,"E3.0.5.0"),sQuery(id+"F0.wireOp",EDGE,"E3.0.5.1"),sQuery(id+"F0.wireOp",EDGE,"E3.0.5.2"),sQuery(id+"F0.wireOp",EDGE,"E3.0.5.3"),sQuery(id+"F0.wireOp",EDGE,"E3.1.1.0"),sQuery(id+"F0.wireOp",EDGE,"E3.1.1.1"),sQuery(id+"F0.wireOp",EDGE,"E3.1.1.2"),sQuery(id+"F0.wireOp",EDGE,"E3.1.1.3"),sQuery(id+"F0.wireOp",EDGE,"E3.1.2.0"),sQuery(id+"F0.wireOp",EDGE,"E3.1.2.1"),sQuery(id+"F0.wireOp",EDGE,"E3.1.2.2"),sQuery(id+"F0.wireOp",EDGE,"E3.1.2.3"),sQuery(id+"F0.wireOp",EDGE,"E3.1.3.0"),sQuery(id+"F0.wireOp",EDGE,"E3.1.3.1"),sQuery(id+"F0.wireOp",EDGE,"E3.1.3.2"),sQuery(id+"F0.wireOp",EDGE,"E3.1.3.3"),sQuery(id+"F0.wireOp",EDGE,"E3.1.4.0"),sQuery(id+"F0.wireOp",EDGE,"E3.1.4.1"),sQuery(id+"F0.wireOp",EDGE,"E3.1.4.2"),sQuery(id+"F0.wireOp",EDGE,"E3.1.4.3"),sQuery(id+"F0.wireOp",EDGE,"E3.1.5.0"),sQuery(id+"F0.wireOp",EDGE,"E3.1.5.1"),sQuery(id+"F0.wireOp",EDGE,"E3.1.5.2"),sQuery(id+"F0.wireOp",EDGE,"E3.1.5.3"),sQuery(id+"F0.wireOp",EDGE,"E3.1.6.0"),sQuery(id+"F0.wireOp",EDGE,"E3.1.6.1"),sQuery(id+"F0.wireOp",EDGE,"E3.1.6.2"),sQuery(id+"F0.wireOp",EDGE,"E3.1.6.3"),sQuery(id+"F0.wireOp",EDGE,"E3.2.0.0"),sQuery(id+"F0.wireOp",EDGE,"E3.2.0.1"),sQuery(id+"F0.wireOp",EDGE,"E3.2.0.2"),sQuery(id+"F0.wireOp",EDGE,"E3.2.0.3"),sQuery(id+"F0.wireOp",EDGE,"E3.2.1.0"),sQuery(id+"F0.wireOp",EDGE,"E3.2.1.1"),sQuery(id+"F0.wireOp",EDGE,"E3.2.1.2"),sQuery(id+"F0.wireOp",EDGE,"E3.2.1.3"),sQuery(id+"F0.wireOp",EDGE,"E3.2.2.0"),sQuery(id+"F0.wireOp",EDGE,"E3.2.2.1"),sQuery(id+"F0.wireOp",EDGE,"E3.2.2.2"),sQuery(id+"F0.wireOp",EDGE,"E3.2.2.3"),sQuery(id+"F0.wireOp",EDGE,"E3.2.3.0"),sQuery(id+"F0.wireOp",EDGE,"E3.2.3.1"),sQuery(id+"F0.wireOp",EDGE,"E3.2.3.2"),sQuery(id+"F0.wireOp",EDGE,"E3.2.3.3"),sQuery(id+"F0.wireOp",EDGE,"E3.2.4.0"),sQuery(id+"F0.wireOp",EDGE,"E3.2.4.1"),sQuery(id+"F0.wireOp",EDGE,"E3.2.4.2"),sQuery(id+"F0.wireOp",EDGE,"E3.2.4.3"),sQuery(id+"F0.wireOp",EDGE,"E3.2.5.0"),sQuery(id+"F0.wireOp",EDGE,"E3.2.5.1"),sQuery(id+"F0.wireOp",EDGE,"E3.2.5.2"),sQuery(id+"F0.wireOp",EDGE,"E3.2.5.3"),sQuery(id+"F0.wireOp",EDGE,"E3.2.6.0"),sQuery(id+"F0.wireOp",EDGE,"E3.2.6.1"),sQuery(id+"F0.wireOp",EDGE,"E3.2.6.2"),sQuery(id+"F0.wireOp",EDGE,"E3.2.6.3"),sQuery(id+"F0.wireOp",EDGE,"E3.2.7.0"),sQuery(id+"F0.wireOp",EDGE,"E3.2.7.1"),sQuery(id+"F0.wireOp",EDGE,"E3.2.7.2"),sQuery(id+"F0.wireOp",EDGE,"E3.2.7.3"),sQuery(id+"F0.wireOp",EDGE,"E3.3.0.0"),sQuery(id+"F0.wireOp",EDGE,"E3.3.0.1"),sQuery(id+"F0.wireOp",EDGE,"E3.3.0.2"),sQuery(id+"F0.wireOp",EDGE,"E3.3.0.3"),sQuery(id+"F0.wireOp",EDGE,"E3.3.1.0"),sQuery(id+"F0.wireOp",EDGE,"E3.3.1.1"),sQuery(id+"F0.wireOp",EDGE,"E3.3.1.2"),sQuery(id+"F0.wireOp",EDGE,"E3.3.1.3"),sQuery(id+"F0.wireOp",EDGE,"E3.3.2.0"),sQuery(id+"F0.wireOp",EDGE,"E3.3.2.1"),sQuery(id+"F0.wireOp",EDGE,"E3.3.2.2"),sQuery(id+"F0.wireOp",EDGE,"E3.3.2.3"),sQuery(id+"F0.wireOp",EDGE,"E3.3.3.0"),sQuery(id+"F0.wireOp",EDGE,"E3.3.3.1"),sQuery(id+"F0.wireOp",EDGE,"E3.3.3.2"),sQuery(id+"F0.wireOp",EDGE,"E3.3.3.3"),sQuery(id+"F0.wireOp",EDGE,"E3.3.4.0"),sQuery(id+"F0.wireOp",EDGE,"E3.3.4.1"),sQuery(id+"F0.wireOp",EDGE,"E3.3.4.2"),sQuery(id+"F0.wireOp",EDGE,"E3.3.4.3"),sQuery(id+"F0.wireOp",EDGE,"E3.3.5.0"),sQuery(id+"F0.wireOp",EDGE,"E3.3.5.1"),sQuery(id+"F0.wireOp",EDGE,"E3.3.5.2"),sQuery(id+"F0.wireOp",EDGE,"E3.3.5.3"),sQuery(id+"F0.wireOp",EDGE,"E3.3.6.0"),sQuery(id+"F0.wireOp",EDGE,"E3.3.6.1"),sQuery(id+"F0.wireOp",EDGE,"E3.3.6.2"),sQuery(id+"F0.wireOp",EDGE,"E3.3.6.3"),sQuery(id+"F0.wireOp",EDGE,"E3.3.7.0"),sQuery(id+"F0.wireOp",EDGE,"E3.3.7.1"),sQuery(id+"F0.wireOp",EDGE,"E3.3.7.2"),sQuery(id+"F0.wireOp",EDGE,"E3.3.7.3"),sQuery(id+"F0.wireOp",EDGE,"E3.4.0.0"),sQuery(id+"F0.wireOp",EDGE,"E3.4.0.1"),sQuery(id+"F0.wireOp",EDGE,"E3.4.0.2"),sQuery(id+"F0.wireOp",EDGE,"E3.4.0.3"),sQuery(id+"F0.wireOp",EDGE,"E3.4.1.0"),sQuery(id+"F0.wireOp",EDGE,"E3.4.1.1"),sQuery(id+"F0.wireOp",EDGE,"E3.4.1.2"),sQuery(id+"F0.wireOp",EDGE,"E3.4.1.3"),sQuery(id+"F0.wireOp",EDGE,"E3.4.2.0"),sQuery(id+"F0.wireOp",EDGE,"E3.4.2.1"),sQuery(id+"F0.wireOp",EDGE,"E3.4.2.2"),sQuery(id+"F0.wireOp",EDGE,"E3.4.2.3"),sQuery(id+"F0.wireOp",EDGE,"E3.4.3.0"),sQuery(id+"F0.wireOp",EDGE,"E3.4.3.1"),sQuery(id+"F0.wireOp",EDGE,"E3.4.3.2"),sQuery(id+"F0.wireOp",EDGE,"E3.4.3.3"),sQuery(id+"F0.wireOp",EDGE,"E3.4.4.0"),sQuery(id+"F0.wireOp",EDGE,"E3.4.4.1"),sQuery(id+"F0.wireOp",EDGE,"E3.4.4.2"),sQuery(id+"F0.wireOp",EDGE,"E3.4.4.3"),sQuery(id+"F0.wireOp",EDGE,"E3.4.5.0"),sQuery(id+"F0.wireOp",EDGE,"E3.4.5.1"),sQuery(id+"F0.wireOp",EDGE,"E3.4.5.2"),sQuery(id+"F0.wireOp",EDGE,"E3.4.5.3"),sQuery(id+"F0.wireOp",EDGE,"E3.4.6.0"),sQuery(id+"F0.wireOp",EDGE,"E3.4.6.1"),sQuery(id+"F0.wireOp",EDGE,"E3.4.6.2"),sQuery(id+"F0.wireOp",EDGE,"E3.4.6.3"),sQuery(id+"F0.wireOp",EDGE,"E3.4.7.0"),sQuery(id+"F0.wireOp",EDGE,"E3.4.7.1"),sQuery(id+"F0.wireOp",EDGE,"E3.4.7.2"),sQuery(id+"F0.wireOp",EDGE,"E3.4.7.3"),sQuery(id+"F0.wireOp",EDGE,"E3.5.0.0"),sQuery(id+"F0.wireOp",EDGE,"E3.5.0.1"),sQuery(id+"F0.wireOp",EDGE,"E3.5.0.2"),sQuery(id+"F0.wireOp",EDGE,"E3.5.0.3"),sQuery(id+"F0.wireOp",EDGE,"E3.5.1.0"),sQuery(id+"F0.wireOp",EDGE,"E3.5.1.1"),sQuery(id+"F0.wireOp",EDGE,"E3.5.1.2"),sQuery(id+"F0.wireOp",EDGE,"E3.5.1.3"),sQuery(id+"F0.wireOp",EDGE,"E3.5.2.0"),sQuery(id+"F0.wireOp",EDGE,"E3.5.2.1"),sQuery(id+"F0.wireOp",EDGE,"E3.5.2.2"),sQuery(id+"F0.wireOp",EDGE,"E3.5.2.3"),sQuery(id+"F0.wireOp",EDGE,"E3.5.3.0"),sQuery(id+"F0.wireOp",EDGE,"E3.5.3.1"),sQuery(id+"F0.wireOp",EDGE,"E3.5.3.2"),sQuery(id+"F0.wireOp",EDGE,"E3.5.3.3"),sQuery(id+"F0.wireOp",EDGE,"E3.5.4.0"),sQuery(id+"F0.wireOp",EDGE,"E3.5.4.1"),sQuery(id+"F0.wireOp",EDGE,"E3.5.4.2"),sQuery(id+"F0.wireOp",EDGE,"E3.5.4.3"),sQuery(id+"F0.wireOp",EDGE,"E3.5.5.0"),sQuery(id+"F0.wireOp",EDGE,"E3.5.5.1"),sQuery(id+"F0.wireOp",EDGE,"E3.5.5.2"),sQuery(id+"F0.wireOp",EDGE,"E3.5.5.3"),sQuery(id+"F0.wireOp",EDGE,"E3.5.6.0"),sQuery(id+"F0.wireOp",EDGE,"E3.5.6.1"),sQuery(id+"F0.wireOp",EDGE,"E3.5.6.2"),sQuery(id+"F0.wireOp",EDGE,"E3.5.6.3"),sQuery(id+"F0.wireOp",EDGE,"E3.5.7.0"),sQuery(id+"F0.wireOp",EDGE,"E3.5.7.1"),sQuery(id+"F0.wireOp",EDGE,"E3.5.7.2"),sQuery(id+"F0.wireOp",EDGE,"E3.5.7.3"),sQuery(id+"F0.wireOp",EDGE,"E3.6.1.0"),sQuery(id+"F0.wireOp",EDGE,"E3.6.1.1"),sQuery(id+"F0.wireOp",EDGE,"E3.6.1.2"),sQuery(id+"F0.wireOp",EDGE,"E3.6.1.3"),sQuery(id+"F0.wireOp",EDGE,"E3.6.2.0"),sQuery(id+"F0.wireOp",EDGE,"E3.6.2.1"),sQuery(id+"F0.wireOp",EDGE,"E3.6.2.2"),sQuery(id+"F0.wireOp",EDGE,"E3.6.2.3"),sQuery(id+"F0.wireOp",EDGE,"E3.6.3.0"),sQuery(id+"F0.wireOp",EDGE,"E3.6.3.1"),sQuery(id+"F0.wireOp",EDGE,"E3.6.3.2"),sQuery(id+"F0.wireOp",EDGE,"E3.6.3.3"),sQuery(id+"F0.wireOp",EDGE,"E3.6.4.0"),sQuery(id+"F0.wireOp",EDGE,"E3.6.4.1"),sQuery(id+"F0.wireOp",EDGE,"E3.6.4.2"),sQuery(id+"F0.wireOp",EDGE,"E3.6.4.3"),sQuery(id+"F0.wireOp",EDGE,"E3.6.5.0"),sQuery(id+"F0.wireOp",EDGE,"E3.6.5.1"),sQuery(id+"F0.wireOp",EDGE,"E3.6.5.2"),sQuery(id+"F0.wireOp",EDGE,"E3.6.5.3"),sQuery(id+"F0.wireOp",EDGE,"E3.6.6.0"),sQuery(id+"F0.wireOp",EDGE,"E3.6.6.1"),sQuery(id+"F0.wireOp",EDGE,"E3.6.6.2"),sQuery(id+"F0.wireOp",EDGE,"E3.6.6.3"),sQuery(id+"F0.wireOp",EDGE,"E3.7.2.0"),sQuery(id+"F0.wireOp",EDGE,"E3.7.2.1"),sQuery(id+"F0.wireOp",EDGE,"E3.7.2.2"),sQuery(id+"F0.wireOp",EDGE,"E3.7.2.3"),sQuery(id+"F0.wireOp",EDGE,"E3.7.5.0"),sQuery(id+"F0.wireOp",EDGE,"E3.7.5.1"),sQuery(id+"F0.wireOp",EDGE,"E3.7.5.2"),sQuery(id+"F0.wireOp",EDGE,"E3.7.5.3")])]});
            hole(context, id + "F3", {"style" : HoleStyle.C_SINK, "endStyle" : HoleEndStyle.BLIND, "standardTappedOrClearance" : lookupTablePath({ "standard" : "ANSI", "fit" : "Normal (ASME)", "size" : "1/4", "type" : "Clearance" }), "standardBlindInLast" : lookupTablePath({ "fit" : "Free", "standard" : "ANSI", "size" : "1/4", "type" : "Clearance" }), "holeDiameter" : 6.76 * mm, "cSinkDiameter" : 13.5 * mm, "cSinkAngle" : 82 * degree, "holeDepth" : 13.97 * mm, "isTappedThrough" : true, "tappedDepth" : 10.16 * mm, "tapClearance" : 3, "locations" : qUnion([Q0, Q1]), "scope" : qUnion([Q2])});
        }
        {
            var Q0;
            Q0=qCreatedBy(makeId("Top.planeOp"),FACE);
            var sketch = newSketch(context, id + "F4", { "sketchPlane" : qUnion([Q0])});
            skCircle(sketch, "E12", {"center": v(0, 0) * mm, "radius": 63.5 * mm});
            skSolve(sketch);
        }
        {
            var Q0;
            Q0=qCreatedBy(makeId("Top.planeOp"),FACE);
            cPlane(context, id + "F5", {"entities" : qUnion([Q0]), "cplaneType" : CPlaneType.OFFSET, "offset" : 76.2 * mm, "width" : 152.4 * mm, "height" : 152.4 * mm});
        }
        {
            var Q0;
            Q0=qCreatedBy(id+"F5.planeOp",FACE);
            var sketch = newSketch(context, id + "F6", { "sketchPlane" : qUnion([Q0])});
            skCircle(sketch, "E13", {"center": v(0, 0) * mm, "radius": 38.1 * mm});
            skSolve(sketch);
        }
        {
            var Q0;
            Q0=makeQuery(id+"F4.imprint","IMPRINT",FACE,{"disambiguationData":[TD([[makeQuery(id+"F4.imprint","IMPRINT",EDGE,{"derivedFrom":sQuery(id+"F4.wireOp",EDGE,"E12")}),1.0]])]});
            var Q1;
            Q1=makeQuery(id+"F6.imprint","IMPRINT",FACE,{"disambiguationData":[TD([[makeQuery(id+"F6.imprint","IMPRINT",EDGE,{"derivedFrom":sQuery(id+"F6.wireOp",EDGE,"E13")}),1.0]])]});
            loft(context, id + "F7", {"sheetProfilesArray" : [{ "sheetProfileEntities" : qUnion([Q0]) }, { "sheetProfileEntities" : qUnion([Q1]) }]});
        }
        {
            var Q0;
            Q0=qCreatedBy(id+"F5.planeOp",FACE);
            cPlane(context, id + "F8", {"entities" : qUnion([Q0]), "cplaneType" : CPlaneType.OFFSET, "offset" : 50.8 * mm, "width" : 152.4 * mm, "height" : 152.4 * mm});
        }
        {
            var Q0;
            Q0=qCreatedBy(id+"F8.planeOp",FACE);
            var sketch = newSketch(context, id + "F9", { "sketchPlane" : qUnion([Q0])});
            skCircle(sketch, "E14", {"center": v(0, 0) * mm, "radius": 63.5 * mm});
            skSolve(sketch);
        }
        {
            var Q1;
            Q1=makeQuery(id+"F7.opLoft","CAP_FACE",FACE,{"disambiguationData":[OSD([makeQuery(id+"F6.imprint","IMPRINT",FACE,{"disambiguationData":[TD([[makeQuery(id+"F6.imprint","IMPRINT",EDGE,{"derivedFrom":sQuery(id+"F6.wireOp",EDGE,"E13")}),1.0]])]})])],"isStart":true});
            var Q2;
            Q2=makeQuery(id+"F9.imprint","IMPRINT",FACE,{"disambiguationData":[TD([[makeQuery(id+"F9.imprint","IMPRINT",EDGE,{"derivedFrom":sQuery(id+"F9.wireOp",EDGE,"E14")}),1.0]])]});
            loft(context, id + "F10", {"operationType" : NewBodyOperationType.ADD, "sheetProfilesArray" : [{ "sheetProfileEntities" : qUnion([Q1]) }, { "sheetProfileEntities" : qUnion([Q2]) }]});
        }
        {
            var Q0;
            {var subQ0=sQuery(id+"F6.wireOp",EDGE,"E13");var subQ1=sQuery(id+"F4.wireOp",EDGE,"E12");Q0=makeQuery(id+"F10.boolean.opBoolean","MERGE",EDGE,{"derivedFrom":[makeQuery(id+"F7.opLoft","MID_CAP_EDGE",EDGE,{"disambiguationData":[OSD([subQ1,subQ0])],"capPos":1.0}),makeQuery(id+"F10.opLoft","MID_CAP_EDGE",EDGE,{"disambiguationData":[OSD([subQ1,subQ0])],"capPos":0.0})]});}
            fillet(context, id + "F11", {"entities" : qUnion([Q0]), "radius" : 12.7 * mm, "tangentPropagation" : true, "allowEdgeOverflow" : false});
        }
        {
            var Q0;
            Q0=qCreatedBy(makeId("Top.planeOp"),FACE);
            var sketch = newSketch(context, id + "F12", { "sketchPlane" : qUnion([Q0])});
            skCircle(sketch, "E15", {"center": v(0, 0) * mm, "radius": 12.7 * mm});
            skSolve(sketch);
        }
        {
            var Q0;
            Q0=qCreatedBy(makeId("Front.planeOp"),FACE);
            var sketch = newSketch(context, id + "F13", { "sketchPlane" : qUnion([Q0])});
            skFitSpline(sketch, "E16", {"points": [v(0, 0) * mm, v(0, 41.72) * mm, v(24.2, 56.34) * mm, v(64.6, 31.1) * mm, v(82.4, 0) * mm], "startDerivative": vector(-29.03, 175.74) * mm, "endDerivative": vector(54.95, -127.38) * mm});
            skSolve(sketch);
        }
        {
            var Q0;
            Q0=makeQuery(id+"F12.imprint","IMPRINT",FACE,{"disambiguationData":[TD([[makeQuery(id+"F12.imprint","IMPRINT",EDGE,{"derivedFrom":sQuery(id+"F12.wireOp",EDGE,"E15")}),1.0]])]});
            var Q1;
            Q1=sQuery(id+"F13.wireOp",EDGE,"E16");
            sweep(context, id + "F14", {"profiles" : qUnion([Q0]), "path" : qUnion([Q1])});
        }
        {
            var Q0;
            Q0=qCreatedBy(makeId("Top.planeOp"),FACE);
            var sketch = newSketch(context, id + "F15", { "sketchPlane" : qUnion([Q0])});
            skLineSegment(sketch, "E17.bottom", {"start": v(-50.8, 50.8) * mm, "end": v(50.8, 50.8) * mm});
            skLineSegment(sketch, "E17.top", {"start": v(-50.8, -50.8) * mm, "end": v(50.8, -50.8) * mm});
            skLineSegment(sketch, "E17.left", {"start": v(-50.8, 50.8) * mm, "end": v(-50.8, -50.8) * mm});
            skLineSegment(sketch, "E17.right", {"start": v(50.8, 50.8) * mm, "end": v(50.8, -50.8) * mm});
            skPoint(sketch, "E17.middle", {"position": v(0, 0) * mm});
            skSolve(sketch);
        }
        {
            var Q0;
            Q0=qCreatedBy(makeId("Top.planeOp"),FACE);
            cPlane(context, id + "F16", {"entities" : qUnion([Q0]), "cplaneType" : CPlaneType.OFFSET, "offset" : 101.6 * mm, "width" : 152.4 * mm, "height" : 152.4 * mm});
        }
        {
            var Q0;
            Q0=qCreatedBy(id+"F16.planeOp",FACE);
            var sketch = newSketch(context, id + "F17", { "sketchPlane" : qUnion([Q0])});
            skLineSegment(sketch, "E18.bottom", {"start": v(71.84, 0) * mm, "end": v(0, 71.84) * mm});
            skLineSegment(sketch, "E18.top", {"start": v(0, -71.84) * mm, "end": v(-71.84, 0) * mm});
            skLineSegment(sketch, "E18.left", {"start": v(71.84, 0) * mm, "end": v(0, -71.84) * mm});
            skLineSegment(sketch, "E18.right", {"start": v(0, 71.84) * mm, "end": v(-71.84, 0) * mm});
            skPoint(sketch, "E18.middle", {"position": v(0, 0) * mm});
            skSolve(sketch);
        }
        {
            var Q0;
            Q0=makeQuery(id+"F15.imprint","IMPRINT",FACE,{"disambiguationData":[TD([[makeQuery(id+"F15.imprint","IMPRINT",EDGE,{"derivedFrom":sQuery(id+"F15.wireOp",EDGE,"E17.bottom")}),-1.0]])]});
            var Q1;
            Q1=makeQuery(id+"F17.imprint","IMPRINT",FACE,{"disambiguationData":[TD([[makeQuery(id+"F17.imprint","IMPRINT",EDGE,{"derivedFrom":sQuery(id+"F17.wireOp",EDGE,"E18.bottom")}),1.0]])]});
            loft(context, id + "F18", {"sheetProfilesArray" : [{ "sheetProfileEntities" : qUnion([Q0]) }, { "sheetProfileEntities" : qUnion([Q1]) }]});
        }
    });
